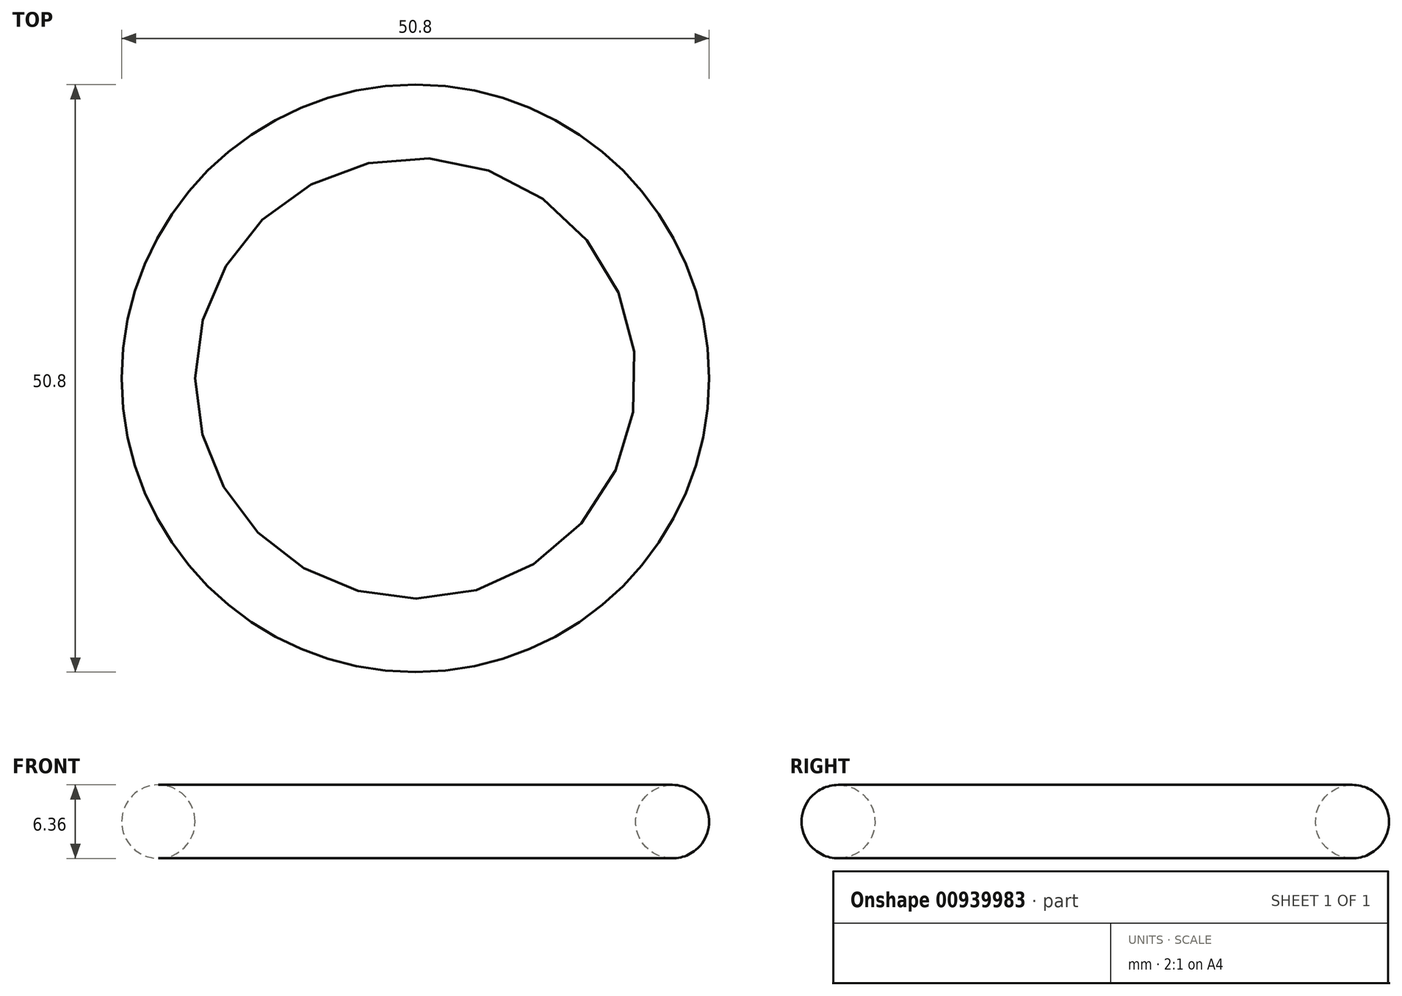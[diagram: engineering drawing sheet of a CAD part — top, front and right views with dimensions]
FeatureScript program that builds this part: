
annotation { "Feature Type Name" : "Feature", "Feature Type Description" : "" }
export const myFeature = defineFeature(function(context is Context, id is Id, definition is map)
    precondition{}
    {
        {
            var Q0;
            Q0=qCreatedBy(makeId("Front.planeOp"),FACE);
            var sketch = newSketch(context, id + "F0", { "sketchPlane" : qUnion([Q0])});
            skCircle(sketch, "E0", {"center": v(-22.23, 0) * mm, "radius": 3.18 * mm});
            skLineSegment(sketch, "E1", {"start": v(-19.05, 0) * mm, "end": v(0, 0) * mm, "construction": true});
            skLineSegment(sketch, "E2", {"start": v(0, 0) * mm, "end": v(0, 7.44) * mm, "construction": true});
            skSolve(sketch);
        }
        {
            var Q0;
            Q0=makeQuery(id+"F0.imprint","IMPRINT",FACE,{"disambiguationData":[TD([[makeQuery(id+"F0.imprint","IMPRINT",EDGE,{"derivedFrom":sQuery(id+"F0.wireOp",EDGE,"E0")}),1.0]])]});
            var Q1;
            Q1=sQuery(id+"F0.wireOp",EDGE,"E2");
            revolve(context, id + "F1", {"surfaceOperationType" : NewSurfaceOperationType.NEW, "entities" : qUnion([Q0]), "axis" : qUnion([Q1]), "revolveType" : RevolveType.FULL});
        }
    });
